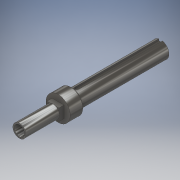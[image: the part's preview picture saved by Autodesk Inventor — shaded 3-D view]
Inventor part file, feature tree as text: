
AUTODESK INVENTOR PART (.ipt)
format: ipt  version: 2019 (Build 230136000, 136)  size: 172,544 bytes
history: native  units: in
note: dims shown in document units (in); Inventor stores cm internally (conversion verified against a paired STEP export)
features: sketch x7, extrude x6, fillet x2, plane x1
ambient origin geometry x8: Origin, YZ Plane, XZ Plane, XY Plane, X Axis, Y Axis, Z Axis, Center Point
bodies: Solid1 (feature_tree)
feature tree (16):
  extrude  "Extrusion1"  Depth=6.125in TaperAngle=0.0deg
  extrude  "Extrusion2"  Depth=0.785in
  extrude  "Extrusion3"  Depth=0.625in
  extrude  "Extrusion4"  Depth=0.225in
  extrude  "Extrusion5"  Depth=0.1125in
  fillet  "Fillet2"  Radius=1.45in
  sketch  "Sketch6"  dims[d21=0.75in d22=0.0in d23=0.1875in]
  plane  "Work Plane1"
  sketch  "Sketch7"
  extrude  "Extrusion6"  Depth=0.1875in
  fillet  "Fillet3"  [1 undecoded]
  sketch  "Sketch1"  dims[d0=1.0in d1=6.125in d2=0.0in]
  sketch  "Sketch2"  dims[d3=0.3125in d4=0.0in d5=0.785in]
  sketch  "Sketch3"  dims[d6=2.0in d7=0.0in d8=0.625in]
  sketch  "Sketch4"  dims[d9=2.0in d10=0.0in d11=0.225in]
  sketch  "Sketch5"  dims[d12=5.1125in d13=0.0in d15=0.1125in d16=1.45in]
note: 1 required parameter value undecoded (feature->parameter linkage not recoverable at this tier; creation-order binding heuristic only, values carry confidence <= 0.55)
